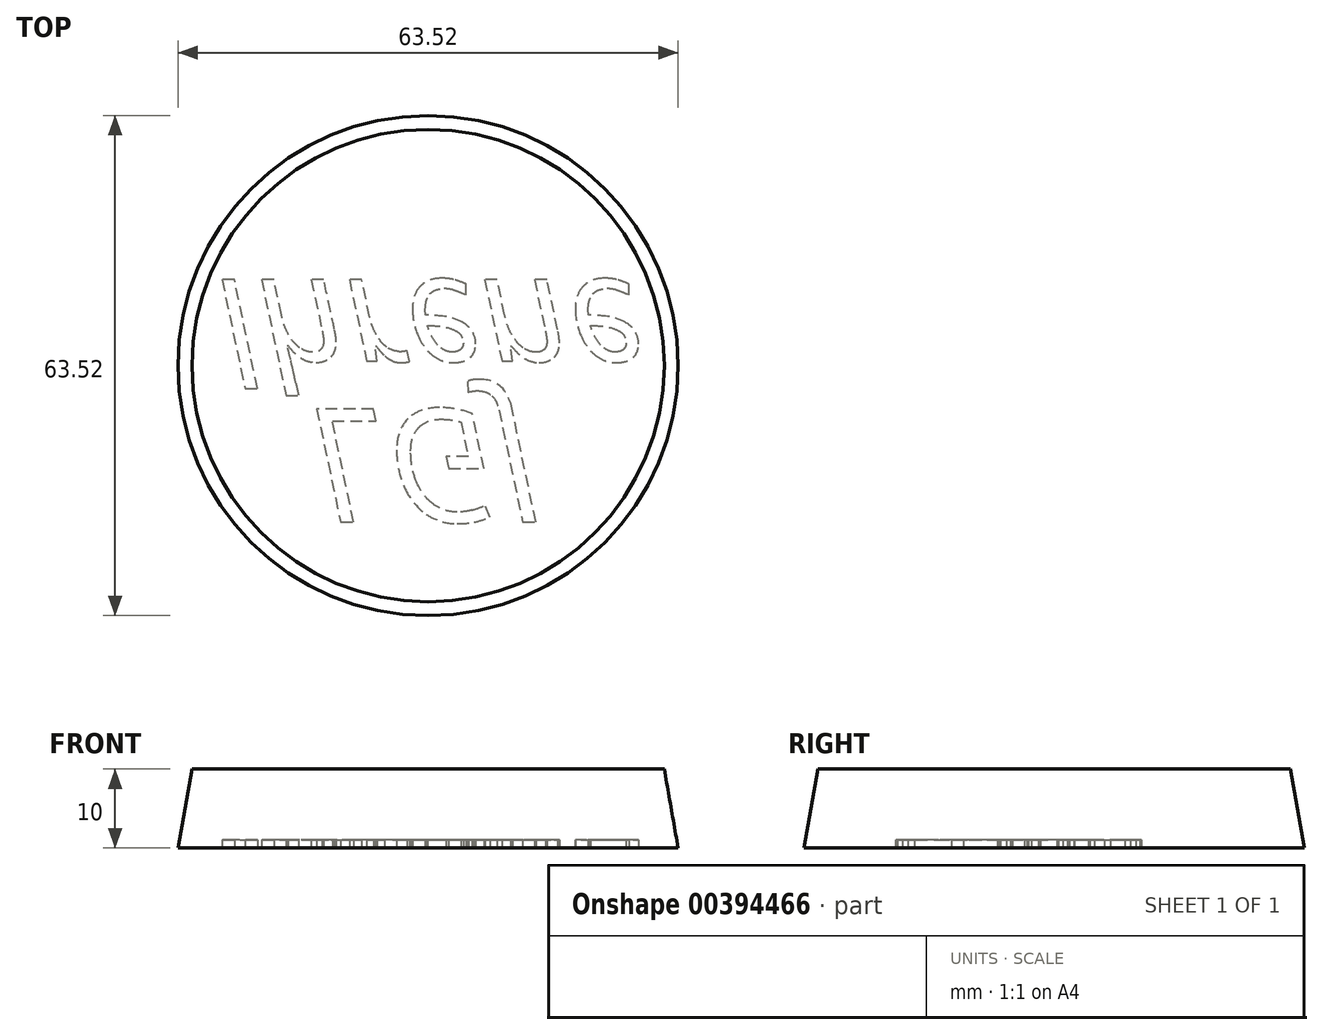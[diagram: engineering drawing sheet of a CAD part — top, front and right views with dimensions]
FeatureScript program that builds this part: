
annotation { "Feature Type Name" : "Feature", "Feature Type Description" : "" }
export const myFeature = defineFeature(function(context is Context, id is Id, definition is map)
    precondition{}
    {
        {
            var Q0;
            Q0=qCreatedBy(makeId("Top.planeOp"),FACE);
            var sketch = newSketch(context, id + "F0", { "sketchPlane" : qUnion([Q0])});
            skCircle(sketch, "E0", {"center": v(0, 0) * mm, "radius": 30 * mm});
            skSolve(sketch);
        }
        {
            var Q0;
            Q0=makeQuery(id+"F0.imprint","IMPRINT",FACE,{"disambiguationData":[TD([[makeQuery(id+"F0.imprint","IMPRINT",EDGE,{"derivedFrom":sQuery(id+"F0.wireOp",EDGE,"E0")}),1.0]])]});
            extrude(context, id + "F1", {"entities" : qUnion([Q0]), "oppositeDirection" : true, "depth" : 10 * mm, "hasDraft" : true, "draftAngle" : 10 * degree});
        }
        {
            var Q0;
            Q0=makeQuery(id+"F1.opExtrude","CAP_FACE",FACE,{"disambiguationData":[OSD([sQuery(id+"F0.wireOp",EDGE,"E0")])],"isStart":false});
            var sketch = newSketch(context, id + "F2", { "sketchPlane" : qUnion([Q0])});
            skText(sketch, "E1", { "text": "LGJ", "fontName": "OpenSans-Italic.ttf"});
            skText(sketch, "E2", { "text": "Ihrene", "fontName": "OpenSans-Italic.ttf"});
            const initialGuessF2  = {"E1": [-0.015, 0.00552, 1, 0, 0.01448], "E2": [-0.027, -0.01092, 1, 0, 0.01392]};
            skSetInitialGuess(sketch, initialGuessF2);
            skSolve(sketch);
        }
        {
            var Q0;
            Q0=qSketchRegion(id+"F2",true);
            extrude(context, id + "F3", {"entities" : qUnion([Q0]), "operationType" : NewBodyOperationType.REMOVE, "oppositeDirection" : true, "depth" : 1 * mm});
        }
    });
